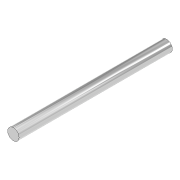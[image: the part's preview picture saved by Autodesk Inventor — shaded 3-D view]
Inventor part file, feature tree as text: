
AUTODESK INVENTOR PART (.ipt)
format: ipt  version: 2020 (Build 240168000, 168)  size: 76,800 bytes
history: native  units: in
note: dims shown in document units (in); Inventor stores cm internally (conversion verified against a paired STEP export)
features: extrude x1, sketch x1
ambient origin geometry x8: Origin, YZ Plane, XZ Plane, XY Plane, X Axis, Y Axis, Z Axis, Center Point
bodies: Solid1 (feature_tree)
feature tree (2):
  extrude  "Extrusion1"  Depth=2.6496in TaperAngle=0.0deg
  sketch  "Sketch1"  dims[d0=0.1969in d1=2.6496in d2=0.0in]
